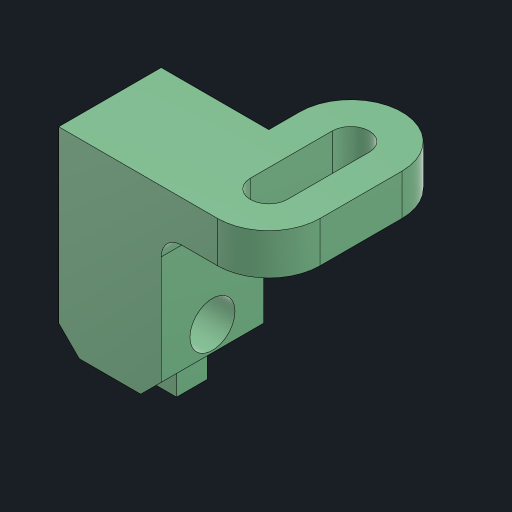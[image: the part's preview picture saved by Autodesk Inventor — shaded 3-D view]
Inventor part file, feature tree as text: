
AUTODESK INVENTOR PART (.ipt)
format: ipt  version: 2023 (Build 270158000, 158)  size: 191,488 bytes
history: native  units: mm
features: sketch x3, extrude x3, other x2, hole x1, fillet x1, chamfer x1
ambient origin geometry x8: Origin, YZ Plane, XZ Plane, XY Plane, X Axis, Y Axis, Z Axis, Center Point
bodies: Body1 (feature_tree)
feature tree (11):
  other  "ソリッド1"
  sketch  "スケッチ1"
  extrude  "押し出し1"  Depth=1.8mm
  extrude  "押し出し4"  Depth=4.0mm
  hole  "穴2"  [1 undecoded]
  fillet  "フィレット2"  Radius=2.0mm
  other  "作業平面2"
  chamfer  "面取り1"  Distance=5.0mm
  extrude  "押し出し5"  Depth=5.25mm
  sketch  "スケッチ5"
  sketch  "スケッチ6"
note: 1 required parameter value undecoded (feature->parameter linkage not recoverable at this tier; creation-order binding heuristic only, values carry confidence <= 0.55)
